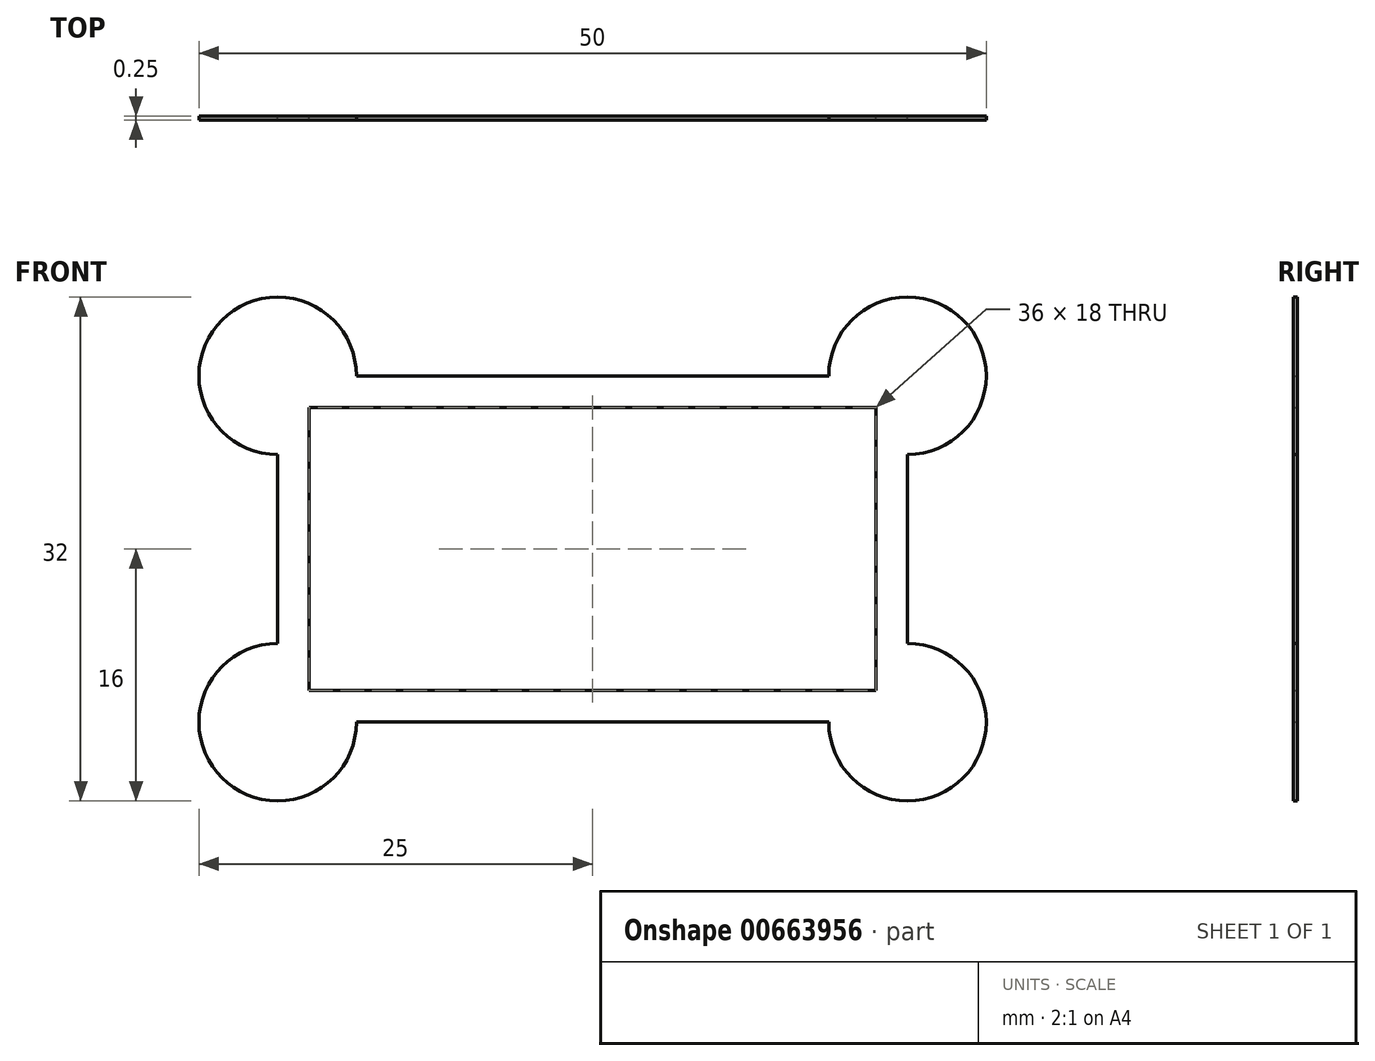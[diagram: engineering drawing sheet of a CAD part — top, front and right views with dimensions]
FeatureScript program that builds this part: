
annotation { "Feature Type Name" : "Feature", "Feature Type Description" : "" }
export const myFeature = defineFeature(function(context is Context, id is Id, definition is map)
    precondition{}
    {
        {
            var Q0;
            Q0=qCreatedBy(makeId("Front.planeOp"),FACE);
            var sketch = newSketch(context, id + "F0", { "sketchPlane" : qUnion([Q0])});
            skLineSegment(sketch, "E0.bottom", {"start": v(-15, 11) * mm, "end": v(15, 11) * mm});
            skLineSegment(sketch, "E0.top", {"start": v(-15, -11) * mm, "end": v(15, -11) * mm});
            skLineSegment(sketch, "E0.left", {"start": v(-20, 6) * mm, "end": v(-20, -6) * mm});
            skLineSegment(sketch, "E0.right", {"start": v(20, 6) * mm, "end": v(20, -6) * mm});
            skPoint(sketch, "E0.middle", {"position": v(0, 0) * mm});
            skArc(sketch, "E1", {"start": v(-15, 11) * mm, "mid": v(-23.54, 14.54) * mm, "end": v(-20, 6) * mm});
            skArc(sketch, "E2", {"start": v(20, 6) * mm, "mid": v(23.54, 14.54) * mm, "end": v(15, 11) * mm});
            skArc(sketch, "E3", {"start": v(15, -11) * mm, "mid": v(23.54, -14.54) * mm, "end": v(20, -6) * mm});
            skArc(sketch, "E4", {"start": v(-20, -6) * mm, "mid": v(-23.54, -14.54) * mm, "end": v(-15, -11) * mm});
            skLineSegment(sketch, "E5.bottom", {"start": v(-18, 9) * mm, "end": v(18, 9) * mm});
            skLineSegment(sketch, "E5.top", {"start": v(-18, -9) * mm, "end": v(18, -9) * mm});
            skLineSegment(sketch, "E5.left", {"start": v(-18, 9) * mm, "end": v(-18, -9) * mm});
            skLineSegment(sketch, "E5.right", {"start": v(18, 9) * mm, "end": v(18, -9) * mm});
            skSolve(sketch);
        }
        {
            var Q0;
            Q0 = qSketchRegion(id + "F0", true);
            extrude(context, id + "F1", {"entities" : qUnion([Q0]), "depth" : 0.25 * mm, "offsetDistance" : 25 * mm});
        }
    });
